# Revit family: HARMANN - Regulatory CAV serii CVD-R
name_source: partatom
category: Akcesoria wentylacyjne
units: mm (PartAtom-declared; Revit-internal decimal feet)

## family parameters
Oparty na płaszczyźnie roboczej = Nie
Tnij formami wycięć po wczytaniu = Nie
Typ części = Dzieli na
Współdzielony = Nie
Wymiar okrągłego złącza = Użyj średnicy
Zawsze pionowo = Nie

## types (16) — shared parameters
Ciśnienie wartość maksymalna = 250.0 Pa
Ciśnienie wartość minimalna = 50.0 Pa
Grubośc uszczelki = 1 mm  [stored 0.00328084 ft]
Komentarze typu = Kanałowy regulator stałego przepływu CAV powietrza
Producent = Harmann Polska Sp. z o.o.
URL = https://harmann.pl
zero-valued in all types: Domyślna rzędna

## per-type parameters (varying)
| type | Autor | DN | DN_Uszczelki | DN_modelu | DN_środek | Długość | Masa | Numer artykułu | Opis | Otwór | Powietrze przepływ maksymalny | Powietrze przepływ minimalny | Uszczelka | b | c | długość początku | obnizenie | rozstaw | rozstaw 2 | wenętrzny promień |
| CVD-R 01 /80 | https://www.archispace.com | 80 mm  [stored 0.262467 ft] | 79 mm | 76 mm  [stored 0.249344 ft] | 73 mm  [stored 0.239501 ft] | 57 mm  [stored 0.187008 ft] | 0.10 kg | 09404100 | Kanałowy regulator CVD-R 01/80. | 2 mm  [stored 0.00656168 ft] | 50.0 m³/h | 15.0 m³/h | 17 mm | 22 mm  [stored 0.0721785 ft] | 19 mm | 22 mm  [stored 0.0721785 ft] | 14 mm  [stored 0.0459318 ft] | 28 mm  [stored 0.0918635 ft] | 25 mm  [stored 0.082021 ft] | 33 mm  [stored 0.108268 ft] |
| CVD-R 02 /100 | https://www.archispace.com | 100 mm | 99 mm | 96 mm | 93 mm  [stored 0.305118 ft] | 68 mm | 0.10 kg | 9413100 | Kanałowy regulator CVD-R 02/100 | 2 mm  [stored 0.00656168 ft] | 100.0 m³/h | 50.0 m³/h | 13 mm | 23 mm  [stored 0.0754593 ft] | 21 mm  [stored 0.0688976 ft] | 22 mm  [stored 0.0721785 ft] | 17 mm | 35 mm  [stored 0.114829 ft] | 32 mm | 40 mm  [stored 0.131234 ft] |
| CVD-R 03 /125 | https://www.archispace.com | 125 mm | 124 mm | 120 mm | 117 mm | 86 mm  [stored 0.282152 ft] | 0.13 kg | 09427100 | Kanałowy regulator CVD-R 03 /125 | 2 mm  [stored 0.00656168 ft] | 180.0 m³/h | 100.0 m³/h | 14 mm  [stored 0.0459318 ft] | 25 mm  [stored 0.082021 ft] | 23 mm  [stored 0.0754593 ft] | 21 mm  [stored 0.0688976 ft] | 21 mm  [stored 0.0688976 ft] | 45 mm  [stored 0.147638 ft] | 42 mm  [stored 0.137795 ft] | 50 mm  [stored 0.164042 ft] |
| CVD-R 04 /160 |  | 160 mm | 159 mm | 159 mm | 155 mm | 85 mm  [stored 0.278871 ft] | 0.25 kg | 09449100 | Kanałowy regulator CVD-R 04 /160 | 3 mm  [stored 0.00984252 ft] | 300.0 m³/h | 180.0 m³/h | 14 mm  [stored 0.0459318 ft] | 40 mm  [stored 0.131234 ft] | 26 mm | 24 mm  [stored 0.0787402 ft] | 30 mm  [stored 0.0984252 ft] | 60 mm  [stored 0.19685 ft] | 57 mm  [stored 0.187008 ft] | 65 mm  [stored 0.213255 ft] |
| CVD-R 05 /200 | https://www.archispace.com | 200 mm | 199 mm | 190 mm | 195 mm | 91 mm  [stored 0.298556 ft] | 0.33 kg | 09468100 | Kanałowy regulator CVD-R 05 /200 | 3 mm  [stored 0.00984252 ft] | 500.0 m³/h | 300.0 m³/h | 13 mm | 50 mm  [stored 0.164042 ft] | 25 mm  [stored 0.082021 ft] | 30 mm  [stored 0.0984252 ft] | 35 mm  [stored 0.114829 ft] | 75 mm | 72 mm | 80 mm  [stored 0.262467 ft] |
| CVD-R 06 /250 |  | 250 mm | 249 mm | 245 mm | 235 mm | 120 mm | 0.33 kg | 09490100 | Kanałowy regulator CVD-R 06 /250 | 3 mm  [stored 0.00984252 ft] | 800.0 m³/h | 500.0 m³/h | 12 mm  [stored 0.0393701 ft] | 60 mm  [stored 0.19685 ft] | 25 mm  [stored 0.082021 ft] | 30 mm  [stored 0.0984252 ft] | 35 mm  [stored 0.114829 ft] | 95 mm  [stored 0.31168 ft] | 92 mm | 100 mm |
| CVD-R 01 /100 | https://www.archispace.com | 100 mm | 99 mm | 96 mm | 93 mm  [stored 0.305118 ft] | 68 mm | 0.10 kg | 09409100 | Kanałowy regulator CVD-R 01/100 | 2 mm  [stored 0.00656168 ft] | 50.0 m³/h | 15.0 m³/h | 13 mm | 23 mm  [stored 0.0754593 ft] | 21 mm  [stored 0.0688976 ft] | 22 mm  [stored 0.0721785 ft] | 17 mm | 35 mm  [stored 0.114829 ft] | 32 mm | 40 mm  [stored 0.131234 ft] |
| CVD-R 02 /125 |  | 125 mm | 124 mm | 120 mm | 117 mm | 86 mm  [stored 0.282152 ft] | 0.13 kg | 09423100 | Kanałowy regulator CVD-R 02 /125 | 2 mm  [stored 0.00656168 ft] | 100.0 m³/h | 50.0 m³/h | 14 mm  [stored 0.0459318 ft] | 25 mm  [stored 0.082021 ft] | 23 mm  [stored 0.0754593 ft] | 21 mm  [stored 0.0688976 ft] | 21 mm  [stored 0.0688976 ft] | 45 mm  [stored 0.147638 ft] | 42 mm  [stored 0.137795 ft] | 50 mm  [stored 0.164042 ft] |
| CVD-R 01 /125 |  | 125 mm | 124 mm | 120 mm | 117 mm | 86 mm  [stored 0.282152 ft] | 0.13 kg | 09419100 | Kanałowy regulator CVD-R 01 /125 | 2 mm  [stored 0.00656168 ft] | 50.0 m³/h | 15.0 m³/h | 14 mm  [stored 0.0459318 ft] | 25 mm  [stored 0.082021 ft] | 23 mm  [stored 0.0754593 ft] | 21 mm  [stored 0.0688976 ft] | 21 mm  [stored 0.0688976 ft] | 45 mm  [stored 0.147638 ft] | 42 mm  [stored 0.137795 ft] | 50 mm  [stored 0.164042 ft] |
| CVD-R 03 /160 |  | 160 mm | 159 mm | 159 mm | 155 mm | 85 mm  [stored 0.278871 ft] | 0.25 kg | 09444100 | Kanałowy regulator CVD-R 03 /160 | 3 mm  [stored 0.00984252 ft] | 180.0 m³/h | 100.0 m³/h | 14 mm  [stored 0.0459318 ft] | 40 mm  [stored 0.131234 ft] | 26 mm | 24 mm  [stored 0.0787402 ft] | 30 mm  [stored 0.0984252 ft] | 60 mm  [stored 0.19685 ft] | 57 mm  [stored 0.187008 ft] | 65 mm  [stored 0.213255 ft] |
| CVD-R 02 /160 |  | 160 mm | 159 mm | 159 mm | 155 mm | 85 mm  [stored 0.278871 ft] | 0.25 kg | 09441100 | Kanałowy regulator CVD-R 02 /160 | 3 mm  [stored 0.00984252 ft] | 100.0 m³/h | 50.0 m³/h | 14 mm  [stored 0.0459318 ft] | 40 mm  [stored 0.131234 ft] | 26 mm | 24 mm  [stored 0.0787402 ft] | 30 mm  [stored 0.0984252 ft] | 60 mm  [stored 0.19685 ft] | 57 mm  [stored 0.187008 ft] | 65 mm  [stored 0.213255 ft] |
| CVD-R 01 /160 |  | 160 mm | 159 mm | 159 mm | 155 mm | 85 mm  [stored 0.278871 ft] | 0.25 kg | 09440100 | Kanałowy regulator CVD-R 01 /160 | 3 mm  [stored 0.00984252 ft] | 50.0 m³/h | 15.0 m³/h | 14 mm  [stored 0.0459318 ft] | 40 mm  [stored 0.131234 ft] | 26 mm | 24 mm  [stored 0.0787402 ft] | 30 mm  [stored 0.0984252 ft] | 60 mm  [stored 0.19685 ft] | 57 mm  [stored 0.187008 ft] | 65 mm  [stored 0.213255 ft] |
| CVD-R 04 /200 |  | 200 mm | 199 mm | 190 mm | 195 mm | 91 mm  [stored 0.298556 ft] | 0.33 kg | 09464100 | Kanałowy regulator CVD-R 04 /200 | 3 mm  [stored 0.00984252 ft] | 300.0 m³/h | 180.0 m³/h | 13 mm | 50 mm  [stored 0.164042 ft] | 25 mm  [stored 0.082021 ft] | 30 mm  [stored 0.0984252 ft] | 35 mm  [stored 0.114829 ft] | 75 mm | 72 mm | 80 mm  [stored 0.262467 ft] |
| CVD-R 03 /200 |  | 200 mm | 199 mm | 190 mm | 195 mm | 91 mm  [stored 0.298556 ft] | 0.33 kg | 09457100 | Kanałowy regulator CVD-R 03 /200 | 3 mm  [stored 0.00984252 ft] | 180.0 m³/h | 100.0 m³/h | 13 mm | 50 mm  [stored 0.164042 ft] | 25 mm  [stored 0.082021 ft] | 30 mm  [stored 0.0984252 ft] | 35 mm  [stored 0.114829 ft] | 75 mm | 72 mm | 80 mm  [stored 0.262467 ft] |
| CVD-R 05 /250 |  | 250 mm | 249 mm | 245 mm | 235 mm | 120 mm | 0.33 kg | 09483100 | Kanałowy regulator CVD-R 05 /250 | 3 mm  [stored 0.00984252 ft] | 500.0 m³/h | 300.0 m³/h | 12 mm  [stored 0.0393701 ft] | 60 mm  [stored 0.19685 ft] | 25 mm  [stored 0.082021 ft] | 30 mm  [stored 0.0984252 ft] | 35 mm  [stored 0.114829 ft] | 95 mm  [stored 0.31168 ft] | 92 mm | 100 mm |
| CVD-R 04 /250 |  | 250 mm | 249 mm | 245 mm | 235 mm | 120 mm | 0.33 kg | 09477100 | Kanałowy regulator CVD-R 04 /250 | 3 mm  [stored 0.00984252 ft] | 300.0 m³/h | 180.0 m³/h | 12 mm  [stored 0.0393701 ft] | 60 mm  [stored 0.19685 ft] | 25 mm  [stored 0.082021 ft] | 30 mm  [stored 0.0984252 ft] | 35 mm  [stored 0.114829 ft] | 95 mm  [stored 0.31168 ft] | 92 mm | 100 mm |

note: column(s) folded — value = type name in every type: Model

note: [stored X ft] marks values corroborated as IEEE doubles in the binary element streams (Revit-internal decimal feet)

## geometry (parser evidence)
native form markers: Sweep x2
no freeform markers — native parametric forms only
